# Revit family: FM1
name_source: partatom
category: Plumbing Fixtures
revit_build: Autodesk Revit Architecture 2012 (Build: 20110309_2315(x64)
units: mm (PartAtom-declared; Revit-internal decimal feet)

## types (1)
- FM1.100
    Assembly Code = D2010
    CW Connection = Yes
    CWFU = 0
    Control stop assembly = C-FMC1.3
    Cost = 0 $
    Default Elevation = 0' - 0"
    Description = Exposed type. Back entry + flush pipe + connector
    Flush pipe = FMT1.1
    Flush pipe coupling nut = C-FM8.14
    HW Connection = Yes
    HWFU = 0
    Handle & nut assembly = C-FMC1.5
    Handle seal = C-FM8.70
    Headpart = C-FM8.32
    Keynote = Flushvalve
    Manufacturer = COBRA
    Material = Chrome - Polished
    Model = FM1.100
    Piston assembly = C-FM8.30
    Plunger assembly = C-FM8.60
    Range = Standard Flushmaster Flushvalves
    Rubber pan connector = C-FMV8.3
    Top cover assembly = C-FMC1.2
    Type Comments = SANS 1240
    URL = http://www.cobra.co.za
    Vent Connection = No
    WFU = 0
    Washer kit = C-FM8.50
    Waste Connection = No

## geometry (parser evidence)
native form markers: Blend x5
no freeform markers — native parametric forms only
